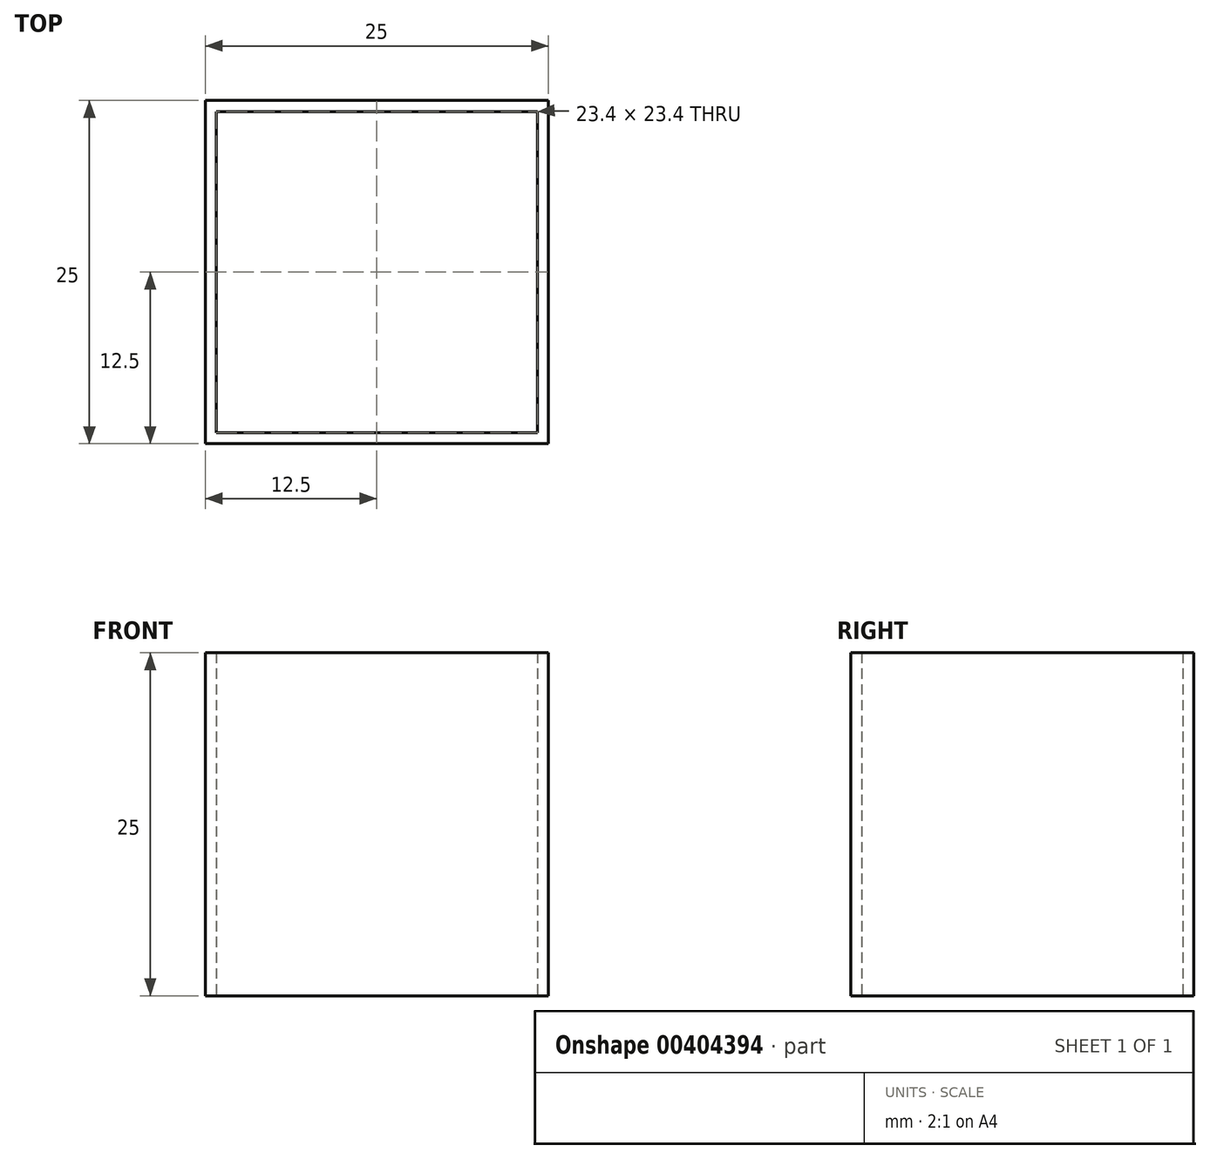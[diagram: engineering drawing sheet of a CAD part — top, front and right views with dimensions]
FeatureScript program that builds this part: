
annotation { "Feature Type Name" : "Feature", "Feature Type Description" : "" }
export const myFeature = defineFeature(function(context is Context, id is Id, definition is map)
    precondition{}
    {
        {
            var Q0;
            Q0=qCreatedBy(makeId("Top.planeOp"),FACE);
            var sketch = newSketch(context, id + "F0", { "sketchPlane" : qUnion([Q0])});
            skLineSegment(sketch, "E0.bottom", {"start": v(12.5, -12.5) * mm, "end": v(-12.5, -12.5) * mm});
            skLineSegment(sketch, "E0.top", {"start": v(12.5, 12.5) * mm, "end": v(-12.5, 12.5) * mm});
            skLineSegment(sketch, "E0.left", {"start": v(12.5, -12.5) * mm, "end": v(12.5, 12.5) * mm});
            skLineSegment(sketch, "E0.right", {"start": v(-12.5, -12.5) * mm, "end": v(-12.5, 12.5) * mm});
            skPoint(sketch, "E0.middle", {"position": v(0, 0) * mm});
            skLineSegment(sketch, "E1.bottom", {"start": v(11.7, -11.7) * mm, "end": v(-11.7, -11.7) * mm});
            skLineSegment(sketch, "E1.top", {"start": v(11.7, 11.7) * mm, "end": v(-11.7, 11.7) * mm});
            skLineSegment(sketch, "E1.left", {"start": v(11.7, -11.7) * mm, "end": v(11.7, 11.7) * mm});
            skLineSegment(sketch, "E1.right", {"start": v(-11.7, -11.7) * mm, "end": v(-11.7, 11.7) * mm});
            skSolve(sketch);
        }
        {
            var Q0;
            Q0=makeQuery(id+"F0.imprint","IMPRINT",FACE,{"disambiguationData":[TD([[makeQuery(id+"F0.imprint","IMPRINT",EDGE,{"derivedFrom":sQuery(id+"F0.wireOp",EDGE,"E0.bottom")}),-1.0]])]});
            extrude(context, id + "F1", {"entities" : qUnion([Q0]), "depth" : 25 * mm});
        }
    });
